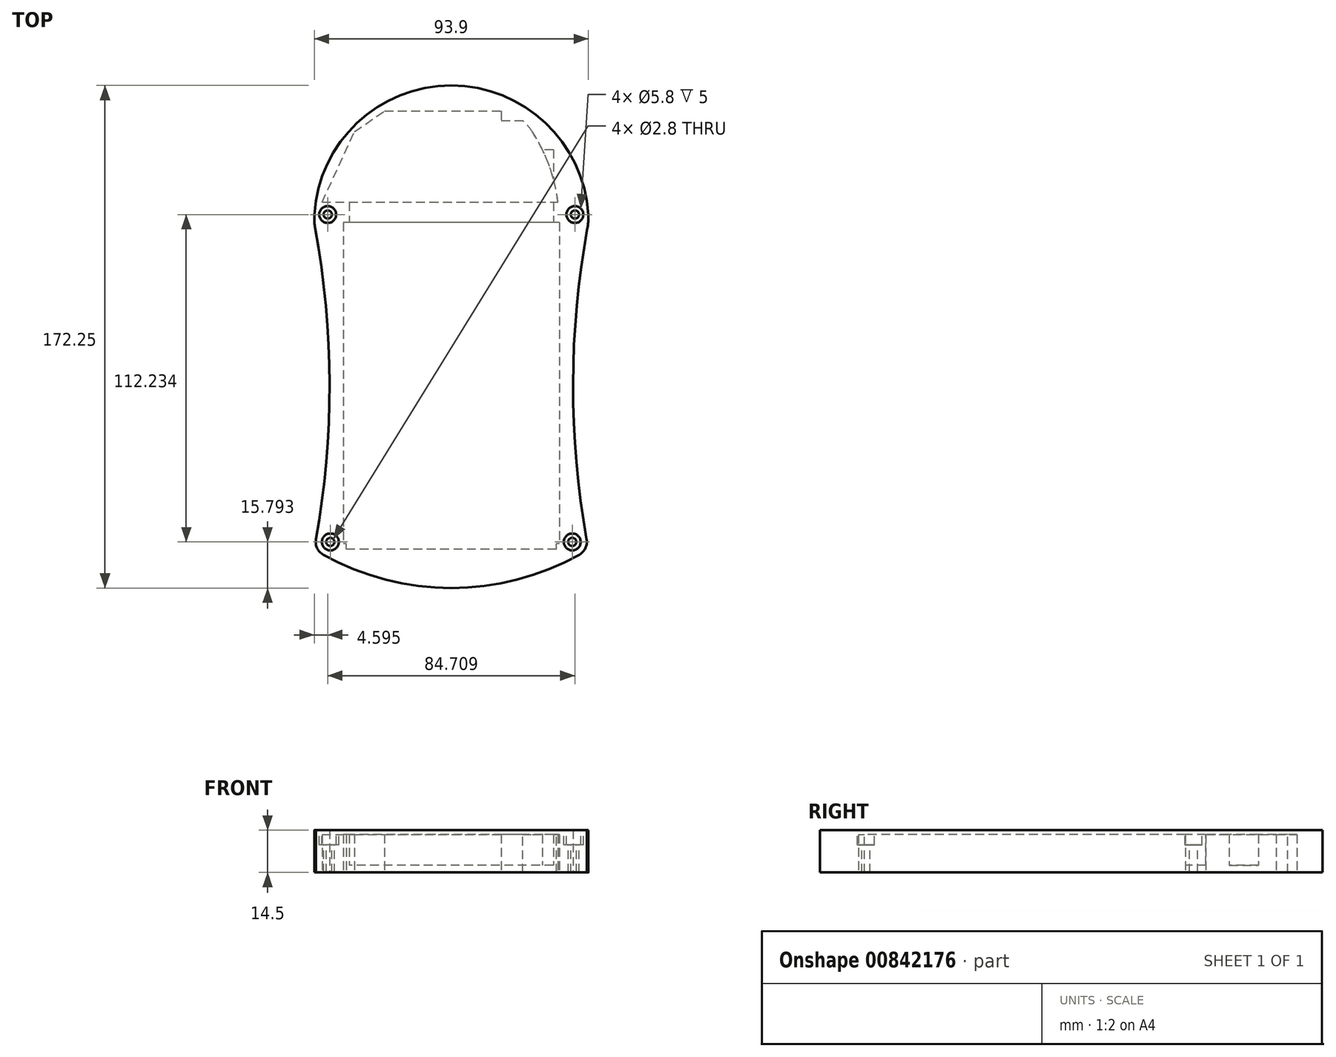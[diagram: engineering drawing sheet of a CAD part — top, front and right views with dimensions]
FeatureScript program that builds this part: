
annotation { "Feature Type Name" : "Feature", "Feature Type Description" : "" }
export const myFeature = defineFeature(function(context is Context, id is Id, definition is map)
    precondition{}
    {
        {
            var Q0;
            Q0=qCreatedBy(makeId("Top.planeOp"),FACE);
            var sketch = newSketch(context, id + "F0", { "sketchPlane" : qUnion([Q0])});
            skLineSegment(sketch, "E0.bottom", {"start": v(36, -56) * mm, "end": v(-36, -56) * mm});
            skLineSegment(sketch, "E0.top", {"start": v(36, 56) * mm, "end": v(-36, 56) * mm});
            skLineSegment(sketch, "E0.left", {"start": v(36, -56) * mm, "end": v(36, 56) * mm});
            skLineSegment(sketch, "E0.right", {"start": v(-36, -56) * mm, "end": v(-36, 56) * mm});
            skPoint(sketch, "E0.middle", {"position": v(0, 0) * mm});
            skArc(sketch, "E1", {"start": v(47, 56) * mm, "mid": v(0, 103) * mm, "end": v(-47, 56) * mm});
            skArc(sketch, "E2", {"start": v(-47, -56) * mm, "mid": v(-41.73, 0) * mm, "end": v(-47, 56) * mm});
            skLineSegment(sketch, "E3", {"start": v(0, 117.63) * mm, "end": v(0, -101.58) * mm, "construction": true});
            skLineSegment(sketch, "E4", {"start": v(-114.42, 0) * mm, "end": v(113.04, 0) * mm, "construction": true});
            skArc(sketch, "E5.MirrorCS", {"start": v(47, -56) * mm, "mid": v(0, -103) * mm, "end": v(-47, -56) * mm});
            skArc(sketch, "E6.MirrorCS", {"start": v(47, -56) * mm, "mid": v(41.73, 0) * mm, "end": v(47, 56) * mm});
            skSolve(sketch);
        }
        {
            var Q0;
            Q0=makeQuery(id+"F0.imprint","IMPRINT",FACE,{"disambiguationData":[TD([[makeQuery(id+"F0.imprint","IMPRINT",EDGE,{"derivedFrom":sQuery(id+"F0.wireOp",EDGE,"E0.bottom")}),1.0]])]});
            extrude(context, id + "F1", {"entities" : qUnion([Q0]), "depth" : 14.5 * mm, "offsetDistance" : 25 * mm});
        }
        {
            var Q0;
            Q0=makeQuery(id+"F1.opExtrude","CAP_FACE",FACE,{"disambiguationData":[OSD([sQuery(id+"F0.wireOp",EDGE,"E0.bottom"),sQuery(id+"F0.wireOp",EDGE,"E0.top"),sQuery(id+"F0.wireOp",EDGE,"E0.left"),sQuery(id+"F0.wireOp",EDGE,"E0.right"),sQuery(id+"F0.wireOp",EDGE,"E1"),sQuery(id+"F0.wireOp",EDGE,"E2"),sQuery(id+"F0.wireOp",EDGE,"E5.MirrorCS"),sQuery(id+"F0.wireOp",EDGE,"E6.MirrorCS")])],"isStart":false});
            var sketch = newSketch(context, id + "F2", { "sketchPlane" : qUnion([Q0])});
            skLineSegment(sketch, "E7.bottom", {"start": v(36, -56) * mm, "end": v(-36, -56) * mm});
            skLineSegment(sketch, "E7.top", {"start": v(36, 56) * mm, "end": v(-36, 56) * mm});
            skLineSegment(sketch, "E7.left", {"start": v(36, -56) * mm, "end": v(36, 56) * mm});
            skLineSegment(sketch, "E7.right", {"start": v(-36, -56) * mm, "end": v(-36, 56) * mm});
            skPoint(sketch, "E7.middle", {"position": v(0, 0) * mm});
            skSolve(sketch);
        }
        {
            var Q0;
            Q0=qSketchRegion(id+"F2",true);
            extrude(context, id + "F3", {"entities" : qUnion([Q0]), "operationType" : NewBodyOperationType.ADD, "oppositeDirection" : true, "depth" : 1.5 * mm, "offsetDistance" : 25 * mm});
        }
        {
            var Q0;
            Q0=makeQuery(id+"F1.opExtrude","CAP_FACE",FACE,{"disambiguationData":[OSD([sQuery(id+"F0.wireOp",EDGE,"E0.bottom"),sQuery(id+"F0.wireOp",EDGE,"E0.top"),sQuery(id+"F0.wireOp",EDGE,"E0.left"),sQuery(id+"F0.wireOp",EDGE,"E0.right"),sQuery(id+"F0.wireOp",EDGE,"E1"),sQuery(id+"F0.wireOp",EDGE,"E2"),sQuery(id+"F0.wireOp",EDGE,"E5.MirrorCS"),sQuery(id+"F0.wireOp",EDGE,"E6.MirrorCS")])],"isStart":true});
            var sketch = newSketch(context, id + "F4", { "sketchPlane" : qUnion([Q0])});
            skLineSegment(sketch, "E8", {"start": v(0, -56) * mm, "end": v(0, 54) * mm, "construction": true});
            skLineSegment(sketch, "E9.bottom", {"start": v(37, -56) * mm, "end": v(-37, -56) * mm});
            skLineSegment(sketch, "E9.top", {"start": v(37, 54) * mm, "end": v(-37, 54) * mm});
            skLineSegment(sketch, "E9.left", {"start": v(37, -56) * mm, "end": v(37, 54) * mm});
            skLineSegment(sketch, "E9.right", {"start": v(-37, -56) * mm, "end": v(-37, 54) * mm});
            skPoint(sketch, "E9.middle", {"position": v(0, -1) * mm});
            skSolve(sketch);
        }
        {
            var Q0;
            Q0=qSketchRegion(id+"F4",true);
            var Q1;
            Q1=makeQuery(id+"F3.opExtrude","CAP_FACE",FACE,{"disambiguationData":[OSD([sQuery(id+"F2.wireOp",EDGE,"E7.bottom"),sQuery(id+"F2.wireOp",EDGE,"E7.top"),sQuery(id+"F2.wireOp",EDGE,"E7.left"),sQuery(id+"F2.wireOp",EDGE,"E7.right")])],"isStart":false});
            extrude(context, id + "F5", {"entities" : qUnion([Q0]), "operationType" : NewBodyOperationType.REMOVE, "endBound" : BoundingType.UP_TO_SURFACE, "oppositeDirection" : true, "depth" : 25 * mm, "endBoundEntityFace" : qUnion([Q1]), "offsetDistance" : 25 * mm});
        }
        {
            var Q0;
            Q0=makeQuery(id+"F1.opExtrude","CAP_FACE",FACE,{"disambiguationData":[OSD([sQuery(id+"F0.wireOp",EDGE,"E0.bottom"),sQuery(id+"F0.wireOp",EDGE,"E0.top"),sQuery(id+"F0.wireOp",EDGE,"E0.left"),sQuery(id+"F0.wireOp",EDGE,"E0.right"),sQuery(id+"F0.wireOp",EDGE,"E1"),sQuery(id+"F0.wireOp",EDGE,"E2"),sQuery(id+"F0.wireOp",EDGE,"E5.MirrorCS"),sQuery(id+"F0.wireOp",EDGE,"E6.MirrorCS")])],"isStart":true});
            var sketch = newSketch(context, id + "F6", { "sketchPlane" : qUnion([Q0])});
            skArc(sketch, "E10", {"start": v(47, 56) * mm, "mid": v(0, 69.25) * mm, "end": v(-47, 56) * mm});
            skArc(sketch, "E11.0", {"start": v(47, 56) * mm, "mid": v(0, 103) * mm, "end": v(-47, 56) * mm});
            skSolve(sketch);
        }
        {
            var Q0;
            Q0=qSketchRegion(id+"F6",true);
            extrude(context, id + "F7", {"entities" : qUnion([Q0]), "operationType" : NewBodyOperationType.REMOVE, "oppositeDirection" : true, "depth" : 25 * mm, "offsetDistance" : 25 * mm});
        }
        {
            var Q0;
            Q0=makeQuery(id+"F1.opExtrude","CAP_FACE",FACE,{"disambiguationData":[OSD([sQuery(id+"F0.wireOp",EDGE,"E0.bottom"),sQuery(id+"F0.wireOp",EDGE,"E0.top"),sQuery(id+"F0.wireOp",EDGE,"E0.left"),sQuery(id+"F0.wireOp",EDGE,"E0.right"),sQuery(id+"F0.wireOp",EDGE,"E1"),sQuery(id+"F0.wireOp",EDGE,"E2"),sQuery(id+"F0.wireOp",EDGE,"E5.MirrorCS"),sQuery(id+"F0.wireOp",EDGE,"E6.MirrorCS")])],"isStart":true});
            var sketch = newSketch(context, id + "F8", { "sketchPlane" : qUnion([Q0])});
            skArc(sketch, "E12", {"start": v(27.76, -87.12) * mm, "mid": v(33.54, -75.56) * mm, "end": v(36.57, -63) * mm});
            skLineSegment(sketch, "E13", {"start": v(0, 109.51) * mm, "end": v(0, -146.95) * mm, "construction": true});
            skArc(sketch, "E14.MirrorCS", {"start": v(-27.76, -87.12) * mm, "mid": v(-33.54, -75.56) * mm, "end": v(-36.57, -63) * mm});
            skLineSegment(sketch, "E15", {"start": v(-36.57, -63) * mm, "end": v(36.57, -63) * mm});
            skPoint(sketch, "E16.orphan", {"position": v(-47, -56) * mm});
            skPoint(sketch, "E17.orphan", {"position": v(47, -56) * mm});
            skPoint(sketch, "E18.orphan", {"position": v(37, -56) * mm});
            skPoint(sketch, "E19.orphan", {"position": v(-37, -56) * mm});
            skArc(sketch, "E20.0", {"start": v(20.57, -93.76) * mm, "mid": v(0, -99) * mm, "end": v(-20.57, -93.76) * mm});
            skPoint(sketch, "E21.orphan", {"position": v(-16, -100.2) * mm});
            skPoint(sketch, "E22.orphan", {"position": v(16, -100.2) * mm});
            skPoint(sketch, "E23.visualSharp", {"position": v(-25, -90.99) * mm});
            skArc(sketch, "E23.filletArc", {"start": v(-27.76, -87.12) * mm, "mid": v(-24.57, -90.89) * mm, "end": v(-20.57, -93.76) * mm});
            skPoint(sketch, "E24.visualSharp", {"position": v(25, -90.99) * mm});
            skArc(sketch, "E24.filletArc", {"start": v(20.57, -93.76) * mm, "mid": v(24.57, -90.89) * mm, "end": v(27.76, -87.12) * mm});
            skSolve(sketch);
        }
        {
            var Q0;
            Q0=qSketchRegion(id+"F8",true);
            extrude(context, id + "F9", {"entities" : qUnion([Q0]), "operationType" : NewBodyOperationType.REMOVE, "oppositeDirection" : true, "depth" : 13 * mm, "offsetDistance" : 25 * mm});
        }
        {
            var Q0;
            Q0=makeQuery(id+"F1.opExtrude","SWEPT_EDGE",EDGE,{"disambiguationData":[OSD([sQuery(id+"F0.wireOp",EDGE,"E1"),sQuery(id+"F0.wireOp",EDGE,"E2")])]});
            var Q1;
            Q1=makeQuery(id+"F1.opExtrude","SWEPT_EDGE",EDGE,{"disambiguationData":[OSD([sQuery(id+"F0.wireOp",EDGE,"E1"),sQuery(id+"F0.wireOp",EDGE,"E6.MirrorCS")])]});
            fillet(context, id + "F10", {"entities" : qUnion([Q0, Q1]), "radius" : 20 * mm, "tangentPropagation" : true, "allowEdgeOverflow" : false});
        }
        {
            var Q0;
            {var subQ0=sQuery(id+"F0.wireOp",EDGE,"E6.MirrorCS");Q0=makeQuery(id+"F7.boolean.opBoolean","MERGE",EDGE,{"derivedFrom":[makeQuery(id+"F1.opExtrude","SWEPT_EDGE",EDGE,{"disambiguationData":[OSD([sQuery(id+"F0.wireOp",EDGE,"E5.MirrorCS"),subQ0])]}),makeQuery(id+"F7.opExtrude","SWEPT_EDGE",EDGE,{"disambiguationData":[OSD([subQ0,sQuery(id+"F6.wireOp",EDGE,"E10"),sQuery(id+"F6.wireOp",EDGE,"E11.0")])]})]});}
            var Q1;
            {var subQ0=sQuery(id+"F0.wireOp",EDGE,"E2");Q1=makeQuery(id+"F7.boolean.opBoolean","MERGE",EDGE,{"derivedFrom":[makeQuery(id+"F1.opExtrude","SWEPT_EDGE",EDGE,{"disambiguationData":[OSD([subQ0,sQuery(id+"F0.wireOp",EDGE,"E5.MirrorCS")])]}),makeQuery(id+"F7.opExtrude","SWEPT_EDGE",EDGE,{"disambiguationData":[OSD([subQ0,sQuery(id+"F6.wireOp",EDGE,"E10"),sQuery(id+"F6.wireOp",EDGE,"E11.0")])]})]});}
            fillet(context, id + "F11", {"entities" : qUnion([Q0, Q1]), "radius" : 5 * mm, "tangentPropagation" : true, "allowEdgeOverflow" : false});
        }
        {
            var Q0;
            Q0=makeQuery(id+"F3.boolean.opBoolean","MERGE",FACE,{"derivedFrom":[makeQuery(id+"F1.opExtrude","CAP_FACE",FACE,{"disambiguationData":[OSD([sQuery(id+"F0.wireOp",EDGE,"E0.bottom"),sQuery(id+"F0.wireOp",EDGE,"E0.top"),sQuery(id+"F0.wireOp",EDGE,"E0.left"),sQuery(id+"F0.wireOp",EDGE,"E0.right"),sQuery(id+"F0.wireOp",EDGE,"E1"),sQuery(id+"F0.wireOp",EDGE,"E2"),sQuery(id+"F0.wireOp",EDGE,"E5.MirrorCS"),sQuery(id+"F0.wireOp",EDGE,"E6.MirrorCS")])],"isStart":false}),makeQuery(id+"F3.opExtrude","CAP_FACE",FACE,{"disambiguationData":[OSD([sQuery(id+"F2.wireOp",EDGE,"E7.bottom"),sQuery(id+"F2.wireOp",EDGE,"E7.top"),sQuery(id+"F2.wireOp",EDGE,"E7.left"),sQuery(id+"F2.wireOp",EDGE,"E7.right")])],"isStart":true})]});
            var sketch = newSketch(context, id + "F12", { "sketchPlane" : qUnion([Q0])});
            skCircle(sketch, "E25", {"center": v(-42.35, 58.78) * mm, "radius": 2.9 * mm});
            skLineSegment(sketch, "E26", {"start": v(0, 101.03) * mm, "end": v(0, -86.28) * mm, "construction": true});
            skCircle(sketch, "E27.MirrorC", {"center": v(42.35, 58.78) * mm, "radius": 2.9 * mm});
            skCircle(sketch, "E28", {"center": v(-41.45, -53.46) * mm, "radius": 2.9 * mm});
            skCircle(sketch, "E29.MirrorC", {"center": v(41.45, -53.46) * mm, "radius": 2.9 * mm});
            skSolve(sketch);
        }
        {
            var Q0;
            Q0=qSketchRegion(id+"F12",true);
            extrude(context, id + "F13", {"entities" : qUnion([Q0]), "operationType" : NewBodyOperationType.REMOVE, "oppositeDirection" : true, "depth" : 5 * mm, "offsetDistance" : 25 * mm});
        }
        {
            var Q0;
            Q0=makeQuery(id+"F13.boolean.opBoolean","COPY",FACE,{"derivedFrom":makeQuery(id+"F13.opExtrude","CAP_FACE",FACE,{"disambiguationData":[OSD([sQuery(id+"F12.wireOp",EDGE,"E25")])],"isStart":false})});
            var sketch = newSketch(context, id + "F14", { "sketchPlane" : qUnion([Q0])});
            skCircle(sketch, "E30", {"center": v(-42.35, 58.78) * mm, "radius": 1.4 * mm});
            skLineSegment(sketch, "E31", {"start": v(0, 85.8) * mm, "end": v(0, -75.06) * mm, "construction": true});
            skCircle(sketch, "E32", {"center": v(-41.45, -53.46) * mm, "radius": 1.4 * mm});
            skCircle(sketch, "E33.MirrorC", {"center": v(42.35, 58.78) * mm, "radius": 1.4 * mm});
            skCircle(sketch, "E34.MirrorC", {"center": v(41.45, -53.46) * mm, "radius": 1.4 * mm});
            skSolve(sketch);
        }
        {
            var Q0;
            Q0=qSketchRegion(id+"F14",true);
            extrude(context, id + "F15", {"entities" : qUnion([Q0]), "operationType" : NewBodyOperationType.REMOVE, "oppositeDirection" : true, "depth" : 25 * mm, "offsetDistance" : 25 * mm});
        }
        {
            var Q0;
            Q0=makeQuery(id+"F5.boolean.opBoolean","MERGE",FACE,{"derivedFrom":[makeQuery(id+"F1.opExtrude","SWEPT_FACE",FACE,{"disambiguationData":[OSD([sQuery(id+"F0.wireOp",EDGE,"E0.top")])]}),makeQuery(id+"F5.opExtrude","SWEPT_FACE",FACE,{"disambiguationData":[OSD([sQuery(id+"F4.wireOp",EDGE,"E9.bottom")])]})]});
            var sketch = newSketch(context, id + "F16", { "sketchPlane" : qUnion([Q0])});
            skLineSegment(sketch, "E35.bottom", {"start": v(-35, 13) * mm, "end": v(35, 13) * mm});
            skLineSegment(sketch, "E35.left", {"start": v(-35, 13) * mm, "end": v(-35, 2.5) * mm});
            skLineSegment(sketch, "E35.right", {"start": v(35, 13) * mm, "end": v(35, 2.5) * mm});
            skPoint(sketch, "E35.middle", {"position": v(0, 6.5) * mm});
            skLineSegment(sketch, "E36", {"start": v(35, 2.5) * mm, "end": v(-35, 2.5) * mm});
            skPoint(sketch, "E37.orphan", {"position": v(35, 0) * mm});
            skPoint(sketch, "E38.orphan", {"position": v(-35, 0) * mm});
            skSolve(sketch);
        }
        {
            var Q0;
            Q0=qSketchRegion(id+"F16",true);
            extrude(context, id + "F17", {"entities" : qUnion([Q0]), "operationType" : NewBodyOperationType.REMOVE, "oppositeDirection" : true, "depth" : 25 * mm, "offsetDistance" : 25 * mm});
        }
        {
            var Q0;
            Q0=makeQuery(id+"F9.boolean.opBoolean","COPY",FACE,{"derivedFrom":makeQuery(id+"F9.opExtrude","CAP_FACE",FACE,{"disambiguationData":[OSD([sQuery(id+"F8.wireOp",EDGE,"E12"),sQuery(id+"F8.wireOp",EDGE,"E14.MirrorCS"),sQuery(id+"F8.wireOp",EDGE,"E15"),sQuery(id+"F8.wireOp",EDGE,"E20.0"),sQuery(id+"F8.wireOp",EDGE,"E23.filletArc"),sQuery(id+"F8.wireOp",EDGE,"E24.filletArc")])],"isStart":false})});
            var sketch = newSketch(context, id + "F18", { "sketchPlane" : qUnion([Q0])});
            skPoint(sketch, "E39", {"position": v(24.45, -91) * mm});
            skLineSegment(sketch, "E40", {"start": v(24.45, -91) * mm, "end": v(-24.45, -91) * mm});
            skArc(sketch, "E41.0", {"start": v(-24.45, -91) * mm, "mid": v(-22.6, -92.5) * mm, "end": v(-20.57, -93.76) * mm});
            skArc(sketch, "E42.0", {"start": v(20.57, -93.76) * mm, "mid": v(0, -99) * mm, "end": v(-20.57, -93.76) * mm});
            skArc(sketch, "E43.0", {"start": v(20.57, -93.76) * mm, "mid": v(22.6, -92.5) * mm, "end": v(24.45, -91) * mm});
            skPoint(sketch, "E44.orphan", {"position": v(-27.76, -87.12) * mm});
            skPoint(sketch, "E45.orphan", {"position": v(27.76, -87.12) * mm});
            skSolve(sketch);
        }
        {
            var Q0;
            Q0=qSketchRegion(id+"F18",true);
            var Q1;
            Q1=makeQuery(id+"F1.opExtrude","CAP_FACE",FACE,{"disambiguationData":[OSD([sQuery(id+"F0.wireOp",EDGE,"E0.bottom"),sQuery(id+"F0.wireOp",EDGE,"E0.top"),sQuery(id+"F0.wireOp",EDGE,"E0.left"),sQuery(id+"F0.wireOp",EDGE,"E0.right"),sQuery(id+"F0.wireOp",EDGE,"E1"),sQuery(id+"F0.wireOp",EDGE,"E2"),sQuery(id+"F0.wireOp",EDGE,"E5.MirrorCS"),sQuery(id+"F0.wireOp",EDGE,"E6.MirrorCS")])],"isStart":true});
            extrude(context, id + "F19", {"entities" : qUnion([Q0]), "operationType" : NewBodyOperationType.ADD, "endBound" : BoundingType.UP_TO_SURFACE, "depth" : 25 * mm, "endBoundEntityFace" : qUnion([Q1]), "offsetDistance" : 25 * mm});
        }
        {
            var Q0;
            {var subQ0=sQuery(id+"F0.wireOp",EDGE,"E6.MirrorCS");var subQ1=sQuery(id+"F0.wireOp",EDGE,"E5.MirrorCS");var subQ2=sQuery(id+"F0.wireOp",EDGE,"E2");var subQ3=sQuery(id+"F0.wireOp",EDGE,"E1");var subQ4=sQuery(id+"F0.wireOp",EDGE,"E0.right");var subQ5=sQuery(id+"F0.wireOp",EDGE,"E0.left");var subQ6=sQuery(id+"F0.wireOp",EDGE,"E0.top");var subQ7=sQuery(id+"F0.wireOp",EDGE,"E0.bottom");Q0=makeQuery(id+"F19.boolean.opBoolean","MERGE",FACE,{"derivedFrom":[makeQuery(id+"F1.opExtrude","CAP_FACE",FACE,{"disambiguationData":[OSD([subQ7,subQ6,subQ5,subQ4,subQ3,subQ2,subQ1,subQ0])],"isStart":true}),makeQuery(id+"F19.opExtrude","CAP_FACE",FACE,{"disambiguationData":[OSD([subQ7,subQ6,subQ5,subQ4,subQ3,subQ2,subQ1,subQ0])],"isStart":false})]});}
            var sketch = newSketch(context, id + "F20", { "sketchPlane" : qUnion([Q0])});
            skLineSegment(sketch, "E46", {"start": v(-40.9, -63) * mm, "end": v(-33.2, -87.12) * mm});
            skLineSegment(sketch, "E47", {"start": v(-22.9, -63) * mm, "end": v(-40.9, -63) * mm});
            skLineSegment(sketch, "E48", {"start": v(-33.2, -87.12) * mm, "end": v(-22.9, -94.26) * mm});
            skLineSegment(sketch, "E49", {"start": v(-22.9, -94.26) * mm, "end": v(17.1, -94.26) * mm});
            skLineSegment(sketch, "E50", {"start": v(17.1, -94.26) * mm, "end": v(17.1, -63) * mm});
            skLineSegment(sketch, "E51", {"start": v(17.1, -63) * mm, "end": v(-22.9, -63) * mm});
            skSolve(sketch);
        }
        {
            var Q0;
            Q0=qSketchRegion(id+"F20",true);
            var Q1;
            {var subQ0=sQuery(id+"F2.wireOp",EDGE,"E7.right");var subQ1=sQuery(id+"F2.wireOp",EDGE,"E7.left");var subQ2=sQuery(id+"F2.wireOp",EDGE,"E7.top");var subQ3=sQuery(id+"F2.wireOp",EDGE,"E7.bottom");Q1=makeQuery(id+"F17.boolean.opBoolean","MERGE",FACE,{"derivedFrom":[makeQuery(id+"F5.boolean.opBoolean","MERGE",FACE,{"derivedFrom":[makeQuery(id+"F3.opExtrude","CAP_FACE",FACE,{"disambiguationData":[OSD([subQ3,subQ2,subQ1,subQ0])],"isStart":false}),makeQuery(id+"F5.opExtrude","CAP_FACE",FACE,{"disambiguationData":[OSD([subQ3,subQ2,subQ1,subQ0])],"isStart":false})]}),makeQuery(id+"F9.boolean.opBoolean","COPY",FACE,{"derivedFrom":makeQuery(id+"F9.opExtrude","CAP_FACE",FACE,{"disambiguationData":[OSD([sQuery(id+"F8.wireOp",EDGE,"E12"),sQuery(id+"F8.wireOp",EDGE,"E14.MirrorCS"),sQuery(id+"F8.wireOp",EDGE,"E15"),sQuery(id+"F8.wireOp",EDGE,"E20.0"),sQuery(id+"F8.wireOp",EDGE,"E23.filletArc"),sQuery(id+"F8.wireOp",EDGE,"E24.filletArc")])],"isStart":false})}),makeQuery(id+"F17.opExtrude","SWEPT_FACE",FACE,{"disambiguationData":[OSD([sQuery(id+"F16.wireOp",EDGE,"E35.bottom")])]})]});}
            extrude(context, id + "F21", {"entities" : qUnion([Q0]), "operationType" : NewBodyOperationType.REMOVE, "endBound" : BoundingType.UP_TO_SURFACE, "oppositeDirection" : true, "depth" : 25 * mm, "endBoundEntityFace" : qUnion([Q1]), "offsetDistance" : 25 * mm});
        }
        {
            var Q0;
            {var subQ0=sQuery(id+"F0.wireOp",EDGE,"E6.MirrorCS");var subQ1=sQuery(id+"F0.wireOp",EDGE,"E5.MirrorCS");var subQ2=sQuery(id+"F0.wireOp",EDGE,"E2");var subQ3=sQuery(id+"F0.wireOp",EDGE,"E1");var subQ4=sQuery(id+"F0.wireOp",EDGE,"E0.right");var subQ5=sQuery(id+"F0.wireOp",EDGE,"E0.left");var subQ6=sQuery(id+"F0.wireOp",EDGE,"E0.top");var subQ7=sQuery(id+"F0.wireOp",EDGE,"E0.bottom");Q0=makeQuery(id+"F19.boolean.opBoolean","MERGE",FACE,{"derivedFrom":[makeQuery(id+"F1.opExtrude","CAP_FACE",FACE,{"disambiguationData":[OSD([subQ7,subQ6,subQ5,subQ4,subQ3,subQ2,subQ1,subQ0])],"isStart":true}),makeQuery(id+"F19.opExtrude","CAP_FACE",FACE,{"disambiguationData":[OSD([subQ7,subQ6,subQ5,subQ4,subQ3,subQ2,subQ1,subQ0])],"isStart":false})]});}
            var sketch = newSketch(context, id + "F22", { "sketchPlane" : qUnion([Q0])});
            skLineSegment(sketch, "E52", {"start": v(-40.9, -63) * mm, "end": v(-44.28, -63) * mm});
            skLineSegment(sketch, "E53", {"start": v(-44.28, -63) * mm, "end": v(-33.2, -87.12) * mm});
            skLineSegment(sketch, "E54.0", {"start": v(-40.9, -63) * mm, "end": v(-33.2, -87.12) * mm});
            skSolve(sketch);
        }
        {
            var Q0;
            Q0=qSketchRegion(id+"F22",true);
            var Q1;
            {var subQ0=sQuery(id+"F16.wireOp",EDGE,"E35.bottom");var subQ1=sQuery(id+"F8.wireOp",EDGE,"E24.filletArc");var subQ2=sQuery(id+"F8.wireOp",EDGE,"E23.filletArc");var subQ3=sQuery(id+"F8.wireOp",EDGE,"E20.0");var subQ4=sQuery(id+"F8.wireOp",EDGE,"E15");var subQ5=sQuery(id+"F8.wireOp",EDGE,"E14.MirrorCS");var subQ6=sQuery(id+"F8.wireOp",EDGE,"E12");var subQ7=sQuery(id+"F2.wireOp",EDGE,"E7.right");var subQ8=sQuery(id+"F2.wireOp",EDGE,"E7.left");var subQ9=sQuery(id+"F2.wireOp",EDGE,"E7.top");var subQ10=sQuery(id+"F2.wireOp",EDGE,"E7.bottom");Q1=makeQuery(id+"F21.boolean.opBoolean","MERGE",FACE,{"derivedFrom":[makeQuery(id+"F17.boolean.opBoolean","MERGE",FACE,{"derivedFrom":[makeQuery(id+"F5.boolean.opBoolean","MERGE",FACE,{"derivedFrom":[makeQuery(id+"F3.opExtrude","CAP_FACE",FACE,{"disambiguationData":[OSD([subQ10,subQ9,subQ8,subQ7])],"isStart":false}),makeQuery(id+"F5.opExtrude","CAP_FACE",FACE,{"disambiguationData":[OSD([subQ10,subQ9,subQ8,subQ7])],"isStart":false})]}),makeQuery(id+"F9.boolean.opBoolean","COPY",FACE,{"derivedFrom":makeQuery(id+"F9.opExtrude","CAP_FACE",FACE,{"disambiguationData":[OSD([subQ6,subQ5,subQ4,subQ3,subQ2,subQ1])],"isStart":false})}),makeQuery(id+"F17.opExtrude","SWEPT_FACE",FACE,{"disambiguationData":[OSD([subQ0])]})]}),makeQuery(id+"F21.opExtrude","CAP_FACE",FACE,{"disambiguationData":[OSD([subQ10,subQ9,subQ8,subQ7,subQ6,subQ5,subQ4,subQ3,subQ2,subQ1,subQ0])],"isStart":false})]});}
            extrude(context, id + "F23", {"entities" : qUnion([Q0]), "operationType" : NewBodyOperationType.REMOVE, "endBound" : BoundingType.UP_TO_SURFACE, "oppositeDirection" : true, "depth" : 25 * mm, "endBoundEntityFace" : qUnion([Q1]), "offsetDistance" : 25 * mm});
        }
    });
